# Revit family: DCST_Счетчик водяной промышленный_СТВХ
name_source: partatom
category: Арматура трубопроводов
units: mm (PartAtom-declared; Revit-internal decimal feet)

## family parameters
Всегда вертикально = Да
На основе рабочей плоскости = Нет
Общий = Нет
При загрузке вырезать с полостями = Нет
Размер круглого соединителя = Использовать диаметр
Тип детали = Вставляется

## types (5) — shared parameters
ADSK_Единица измерения = шт.
ADSK_Завод-изготовитель = Декаст
ADSK_Количество = 1
ADSK_Материал = Декаст_Корпус счетчика темно-синий
LT = СТВХ
URL = https://www.decast.com
ИПД_LoRaWAN = ♦ : LoRaWAN
ИПД_ДГ2 = ♦ : импульсный выход (геркон)
ИПД_Коллектор = ♦ : импульсный выход (открытый коллектор)
ИПД_Нет = ♦ : нет
Изготовитель = Декаст

## per-type parameters (varying)
- СТВХ-50: ADSK_Диаметр условный=50 мм; D=112 мм; D0=160 мм; D1=84 мм; D2=135 мм; R=56 мм; R2=67.5 мм; S=112 мм; W1=166.5 мм; W2=156 мм; f=22 мм; h1=83 мм; h2=22.5 мм; h3=22.5 мм; hm=176 мм; k1=8.5 мм; k2=24 мм; k3=24 мм; k4=6.5 мм; s=11.5 мм; t=75 мм; ws1=88.5 мм; ws2=78 мм; Диаметр условного прохода=50 мм; Монтажная длина=200 мм; УГО_Высота=78 мм; УГО_Длина=156 мм; УГО_Длина линии=22 мм
- СТВХ-65: ADSK_Диаметр условный=65 мм; D=112 мм; D0=180 мм; D1=95 мм; D2=135 мм; R=56 мм; R2=67.5 мм; S=112 мм; W1=166.5 мм; W2=156 мм; f=24 мм; h1=83 мм; h2=22.5 мм; h3=22.5 мм; hm=176 мм; k1=15 мм; k2=17 мм; k3=18 мм; k4=12 мм; s=11.5 мм; t=85 мм; ws1=88.5 мм; ws2=78 мм; Диаметр условного прохода=65 мм; Монтажная длина=200 мм; УГО_Высота=76 мм; УГО_Длина=152 мм; УГО_Длина линии=24 мм
- СТВХ-80: ADSK_Диаметр условный=80 мм; D=112 мм; D0=195 мм; D1=123 мм; D2=135 мм; R=56 мм; R2=67.5 мм; S=112.5 мм; W1=166.5 мм; W2=156 мм; f=24 мм; h1=83 мм; h2=22.5 мм; h3=22.5 мм; hm=176 мм; k1=1 мм; k2=26 мм; k3=26 мм; k4=1 мм; s=11.5 мм; t=95 мм; ws1=88.5 мм; ws2=78 мм; Диаметр условного прохода=80 мм; Монтажная длина=225 мм; УГО_Высота=88.5 мм; УГО_Длина=177 мм; УГО_Длина линии=24 мм
- СТВХ-100: ADSK_Диаметр условный=100 мм; D=120 мм; D0=215 мм; D1=144 мм; D2=135 мм; R=60 мм; R2=67.5 мм; S=125 мм; W1=166.5 мм; W2=156 мм; f=26 мм; h1=83 мм; h2=22.5 мм; h3=22.5 мм; hm=176 мм; k1=1 мм; k2=37 мм; k3=37 мм; k4=1 мм; s=11.5 мм; t=105 мм; ws1=88.5 мм; ws2=78 мм; Диаметр условного прохода=100 мм; Монтажная длина=250 мм; УГО_Высота=99 мм; УГО_Длина=198 мм; УГО_Длина линии=26 мм
- СТВХ-150: ADSK_Диаметр условный=150 мм; D=198 мм; D0=280 мм; D1=205 мм; D2=198 мм; R=99 мм; R2=99 мм; S=160 мм; W1=214 мм; W2=252 мм; f=28 мм; h1=99 мм; h2=28 мм; h3=28 мм; hm=205 мм; k1=1 мм; k2=56 мм; k3=56 мм; k4=1 мм; s=0 мм; t=135 мм; ws1=124 мм; ws2=112.6 мм; Диаметр условного прохода=150 мм; Монтажная длина=300 мм; УГО_Высота=122 мм; УГО_Длина=244 мм; УГО_Длина линии=28 мм
